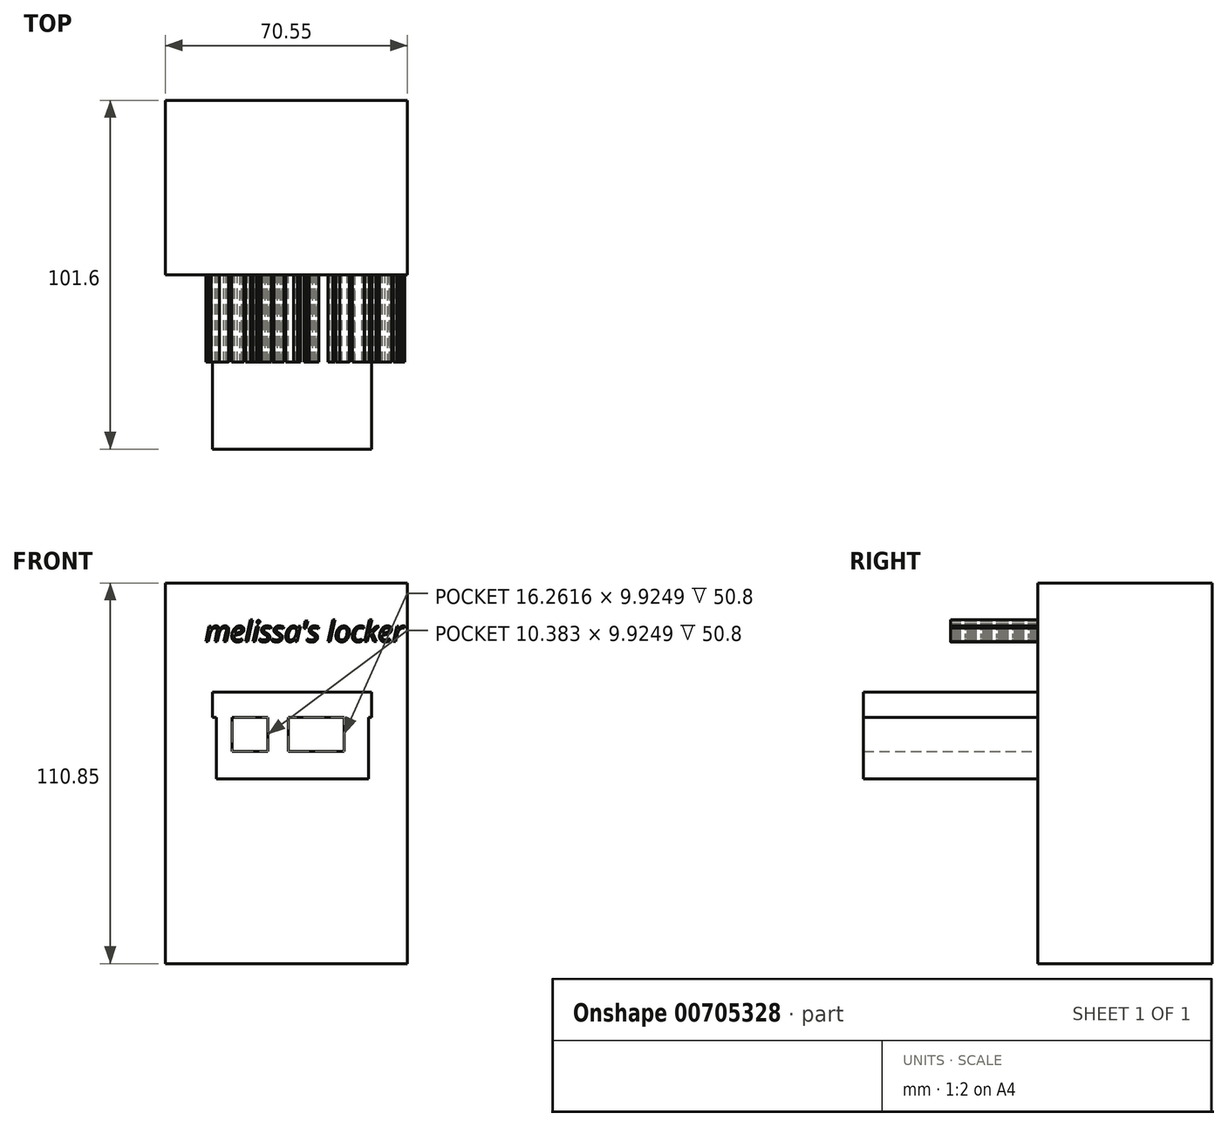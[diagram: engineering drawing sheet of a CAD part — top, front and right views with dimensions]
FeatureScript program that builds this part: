
annotation { "Feature Type Name" : "Feature", "Feature Type Description" : "" }
export const myFeature = defineFeature(function(context is Context, id is Id, definition is map)
    precondition{}
    {
        {
            var Q0;
            Q0=qCreatedBy(makeId("Front.planeOp"),FACE);
            var sketch = newSketch(context, id + "F0", { "sketchPlane" : qUnion([Q0])});
            skLineSegment(sketch, "E0.bottom", {"start": v(-52.07, 49.01) * mm, "end": v(18.48, 49.01) * mm});
            skLineSegment(sketch, "E0.top", {"start": v(-52.07, -61.84) * mm, "end": v(18.48, -61.84) * mm});
            skLineSegment(sketch, "E0.left", {"start": v(-52.07, 49.01) * mm, "end": v(-52.07, -61.84) * mm});
            skLineSegment(sketch, "E0.right", {"start": v(18.48, 49.01) * mm, "end": v(18.48, -61.84) * mm});
            skSolve(sketch);
        }
        {
            var Q0;
            Q0=makeQuery(id+"F0.imprint","IMPRINT",FACE,{"disambiguationData":[TD([[makeQuery(id+"F0.imprint","IMPRINT",EDGE,{"derivedFrom":sQuery(id+"F0.wireOp",EDGE,"E0.bottom")}),-1.0]])]});
            extrude(context, id + "F1", {"entities" : qUnion([Q0]), "depth" : 25.4 * mm, "offsetDistance" : 25.4 * mm});
        }
        {
            var Q0;
            Q0=makeQuery(id+"F1.opExtrude","CAP_FACE",FACE,{"disambiguationData":[OSD([sQuery(id+"F0.wireOp",EDGE,"E0.bottom"),sQuery(id+"F0.wireOp",EDGE,"E0.top"),sQuery(id+"F0.wireOp",EDGE,"E0.left"),sQuery(id+"F0.wireOp",EDGE,"E0.right")])],"isStart":false});
            extrude(context, id + "F2", {"entities" : qUnion([Q0]), "operationType" : NewBodyOperationType.ADD, "depth" : 25.4 * mm, "offsetDistance" : 25.4 * mm});
        }
        {
            var Q0;
            Q0=makeQuery(id+"F2.opExtrude","CAP_FACE",FACE,{"disambiguationData":[OSD([sQuery(id+"F0.wireOp",EDGE,"E0.bottom"),sQuery(id+"F0.wireOp",EDGE,"E0.top"),sQuery(id+"F0.wireOp",EDGE,"E0.left"),sQuery(id+"F0.wireOp",EDGE,"E0.right")])],"isStart":false});
            var sketch = newSketch(context, id + "F3", { "sketchPlane" : qUnion([Q0])});
            skLineSegment(sketch, "E1.bottom", {"start": v(-38.33, 17.25) * mm, "end": v(8.1, 17.25) * mm});
            skLineSegment(sketch, "E1.top", {"start": v(-38.33, 9.92) * mm, "end": v(8.1, 9.92) * mm});
            skLineSegment(sketch, "E1.left", {"start": v(-38.33, 17.25) * mm, "end": v(-38.33, 9.92) * mm});
            skLineSegment(sketch, "E1.right", {"start": v(8.1, 17.25) * mm, "end": v(8.1, 9.92) * mm});
            skSolve(sketch);
        }
        {
            var Q0;
            Q0=makeQuery(id+"F3.imprint","IMPRINT",FACE,{"disambiguationData":[TD([[makeQuery(id+"F3.imprint","IMPRINT",EDGE,{"derivedFrom":sQuery(id+"F3.wireOp",EDGE,"E1.bottom")}),-1.0]])]});
            extrude(context, id + "F4", {"entities" : qUnion([Q0]), "operationType" : NewBodyOperationType.ADD, "depth" : 25.4 * mm, "offsetDistance" : 25.4 * mm});
        }
        {
            var Q0;
            Q0=makeQuery(id+"F4.opExtrude","CAP_FACE",FACE,{"disambiguationData":[OSD([sQuery(id+"F3.wireOp",EDGE,"E1.bottom"),sQuery(id+"F3.wireOp",EDGE,"E1.top"),sQuery(id+"F3.wireOp",EDGE,"E1.left"),sQuery(id+"F3.wireOp",EDGE,"E1.right")])],"isStart":false});
            extrude(context, id + "F5", {"entities" : qUnion([Q0]), "operationType" : NewBodyOperationType.ADD, "depth" : 25.4 * mm, "offsetDistance" : 25.4 * mm});
        }
        {
            var Q0;
            Q0=makeQuery(id+"F2.opExtrude","CAP_FACE",FACE,{"disambiguationData":[OSD([sQuery(id+"F0.wireOp",EDGE,"E0.bottom"),sQuery(id+"F0.wireOp",EDGE,"E0.top"),sQuery(id+"F0.wireOp",EDGE,"E0.left"),sQuery(id+"F0.wireOp",EDGE,"E0.right")])],"isStart":false});
            var sketch = newSketch(context, id + "F6", { "sketchPlane" : qUnion([Q0])});
            skLineSegment(sketch, "E2.bottom", {"start": v(-37.1, 0) * mm, "end": v(7.18, 0) * mm});
            skLineSegment(sketch, "E2.top", {"start": v(-37.1, -8.1) * mm, "end": v(7.18, -8.1) * mm});
            skLineSegment(sketch, "E2.left", {"start": v(-37.1, 0) * mm, "end": v(-37.1, -8.1) * mm});
            skLineSegment(sketch, "E2.right", {"start": v(7.18, 0) * mm, "end": v(7.18, -8.1) * mm});
            skSolve(sketch);
        }
        {
            var Q0;
            Q0=makeQuery(id+"F6.imprint","IMPRINT",FACE,{"disambiguationData":[TD([[makeQuery(id+"F6.imprint","IMPRINT",EDGE,{"derivedFrom":sQuery(id+"F6.wireOp",EDGE,"E2.bottom")}),-1.0]])]});
            extrude(context, id + "F7", {"entities" : qUnion([Q0]), "operationType" : NewBodyOperationType.ADD, "depth" : 25.4 * mm, "offsetDistance" : 25.4 * mm});
        }
        {
            var Q0;
            Q0=makeQuery(id+"F7.opExtrude","CAP_FACE",FACE,{"disambiguationData":[OSD([sQuery(id+"F6.wireOp",EDGE,"E2.bottom"),sQuery(id+"F6.wireOp",EDGE,"E2.top"),sQuery(id+"F6.wireOp",EDGE,"E2.left"),sQuery(id+"F6.wireOp",EDGE,"E2.right")])],"isStart":false});
            extrude(context, id + "F8", {"entities" : qUnion([Q0]), "operationType" : NewBodyOperationType.ADD, "depth" : 25.4 * mm, "offsetDistance" : 25.4 * mm});
        }
        {
            var Q0;
            Q0=makeQuery(id+"F2.opExtrude","CAP_FACE",FACE,{"disambiguationData":[OSD([sQuery(id+"F0.wireOp",EDGE,"E0.bottom"),sQuery(id+"F0.wireOp",EDGE,"E0.top"),sQuery(id+"F0.wireOp",EDGE,"E0.left"),sQuery(id+"F0.wireOp",EDGE,"E0.right")])],"isStart":false});
            var sketch = newSketch(context, id + "F9", { "sketchPlane" : qUnion([Q0])});
            skLineSegment(sketch, "E3.bottom", {"start": v(-31.3, 9.92) * mm, "end": v(-26.42, 9.92) * mm});
            skLineSegment(sketch, "E3.top", {"start": v(-31.3, 0) * mm, "end": v(-26.42, 0) * mm});
            skLineSegment(sketch, "E3.left", {"start": v(-31.3, 9.92) * mm, "end": v(-31.3, 0) * mm});
            skLineSegment(sketch, "E3.right", {"start": v(-26.42, 9.92) * mm, "end": v(-26.42, 0) * mm});
            skLineSegment(sketch, "E4.bottom", {"start": v(-15.12, 9.92) * mm, "end": v(-9, 9.92) * mm});
            skLineSegment(sketch, "E4.top", {"start": v(-15.12, 0) * mm, "end": v(-9, 0) * mm});
            skLineSegment(sketch, "E4.left", {"start": v(-15.12, 9.92) * mm, "end": v(-15.12, 0) * mm});
            skLineSegment(sketch, "E4.right", {"start": v(-9, 9.92) * mm, "end": v(-9, 0) * mm});
            skLineSegment(sketch, "E5.bottom", {"start": v(0, 9.92) * mm, "end": v(7.18, 9.92) * mm});
            skLineSegment(sketch, "E5.top", {"start": v(0, 0) * mm, "end": v(7.18, 0) * mm});
            skLineSegment(sketch, "E5.left", {"start": v(0, 9.92) * mm, "end": v(0, 0) * mm});
            skLineSegment(sketch, "E5.right", {"start": v(7.18, 9.92) * mm, "end": v(7.18, 0) * mm});
            skSolve(sketch);
        }
        {
            var Q0;
            Q0=makeQuery(id+"F9.imprint","IMPRINT",FACE,{"disambiguationData":[TD([[makeQuery(id+"F9.imprint","IMPRINT",EDGE,{"derivedFrom":sQuery(id+"F9.wireOp",EDGE,"E5.bottom")}),-1.0]])]});
            extrude(context, id + "F10", {"entities" : qUnion([Q0]), "operationType" : NewBodyOperationType.ADD, "depth" : 25.4 * mm, "offsetDistance" : 25.4 * mm});
        }
        {
            var Q0;
            Q0=makeQuery(id+"F10.opExtrude","CAP_FACE",FACE,{"disambiguationData":[OSD([sQuery(id+"F9.wireOp",EDGE,"E5.bottom"),sQuery(id+"F9.wireOp",EDGE,"E5.top"),sQuery(id+"F9.wireOp",EDGE,"E5.left"),sQuery(id+"F9.wireOp",EDGE,"E5.right")])],"isStart":false});
            extrude(context, id + "F11", {"entities" : qUnion([Q0]), "operationType" : NewBodyOperationType.ADD, "depth" : 25.4 * mm, "offsetDistance" : 25.4 * mm});
        }
        {
            var Q0;
            Q0=makeQuery(id+"F2.opExtrude","CAP_FACE",FACE,{"disambiguationData":[OSD([sQuery(id+"F0.wireOp",EDGE,"E0.bottom"),sQuery(id+"F0.wireOp",EDGE,"E0.top"),sQuery(id+"F0.wireOp",EDGE,"E0.left"),sQuery(id+"F0.wireOp",EDGE,"E0.right")])],"isStart":false});
            var sketch = newSketch(context, id + "F12", { "sketchPlane" : qUnion([Q0])});
            skLineSegment(sketch, "E6.bottom", {"start": v(-35.88, 9.92) * mm, "end": v(-37.1, 9.92) * mm});
            skLineSegment(sketch, "E6.top", {"start": v(-35.88, 0) * mm, "end": v(-37.1, 0) * mm});
            skLineSegment(sketch, "E7.bottom", {"start": v(-37.1, 9.92) * mm, "end": v(-32.52, 9.92) * mm});
            skLineSegment(sketch, "E7.top", {"start": v(-37.1, 0) * mm, "end": v(-32.52, 0) * mm});
            skLineSegment(sketch, "E7.left", {"start": v(-37.1, 9.92) * mm, "end": v(-37.1, 0) * mm});
            skLineSegment(sketch, "E7.right", {"start": v(-32.52, 9.92) * mm, "end": v(-32.52, 0) * mm});
            skSolve(sketch);
        }
        {
            var Q0;
            {var subQ3=sQuery(id+"F12.wireOp",EDGE,"E7.left");Q0=makeQuery(id+"F12.imprint","IMPRINT",FACE,{"disambiguationData":[TD([[makeQuery(id+"F12.imprint","IMPRINT",EDGE,{"derivedFrom":subQ3}),1.0]])]});}
            extrude(context, id + "F13", {"entities" : qUnion([Q0]), "operationType" : NewBodyOperationType.ADD, "depth" : 25.4 * mm, "offsetDistance" : 25.4 * mm});
        }
        {
            var Q0;
            Q0=makeQuery(id+"F13.opExtrude","CAP_FACE",FACE,{"disambiguationData":[OSD([sQuery(id+"F12.wireOp",EDGE,"E7.bottom"),sQuery(id+"F12.wireOp",EDGE,"E7.top"),sQuery(id+"F12.wireOp",EDGE,"E7.left"),sQuery(id+"F12.wireOp",EDGE,"E7.right")])],"isStart":false});
            extrude(context, id + "F14", {"entities" : qUnion([Q0]), "operationType" : NewBodyOperationType.ADD, "depth" : 25.4 * mm, "offsetDistance" : 25.4 * mm});
        }
        {
            var Q0;
            {var subQ0=sQuery(id+"F6.wireOp",EDGE,"E2.bottom");Q0=makeQuery(id+"F13.boolean.opBoolean","SPLIT",FACE,{"disambiguationData":[TD([makeQuery(id+"F7.opExtrude","SWEPT_FACE",FACE,{"disambiguationData":[OSD([subQ0])]})])],"derivedFrom":makeQuery(id+"F2.opExtrude","CAP_FACE",FACE,{"disambiguationData":[OSD([sQuery(id+"F0.wireOp",EDGE,"E0.bottom"),sQuery(id+"F0.wireOp",EDGE,"E0.top"),sQuery(id+"F0.wireOp",EDGE,"E0.left"),sQuery(id+"F0.wireOp",EDGE,"E0.right")])],"isStart":false})});}
            var sketch = newSketch(context, id + "F15", { "sketchPlane" : qUnion([Q0])});
            skLineSegment(sketch, "E8.bottom", {"start": v(-16.26, 9.92) * mm, "end": v(-22.14, 9.92) * mm});
            skLineSegment(sketch, "E8.top", {"start": v(-16.26, 0) * mm, "end": v(-22.14, 0) * mm});
            skLineSegment(sketch, "E8.left", {"start": v(-16.26, 9.92) * mm, "end": v(-16.26, 0) * mm});
            skLineSegment(sketch, "E8.right", {"start": v(-22.14, 9.92) * mm, "end": v(-22.14, 0) * mm});
            skSolve(sketch);
        }
        {
            var Q0;
            Q0=makeQuery(id+"F15.imprint","IMPRINT",FACE,{"disambiguationData":[TD([[makeQuery(id+"F15.imprint","IMPRINT",EDGE,{"derivedFrom":sQuery(id+"F15.wireOp",EDGE,"E8.bottom")}),-1.0]])]});
            extrude(context, id + "F16", {"entities" : qUnion([Q0]), "operationType" : NewBodyOperationType.ADD, "depth" : 25.4 * mm, "offsetDistance" : 25.4 * mm});
        }
        {
            var Q0;
            Q0=makeQuery(id+"F16.opExtrude","CAP_FACE",FACE,{"disambiguationData":[OSD([sQuery(id+"F15.wireOp",EDGE,"E8.bottom"),sQuery(id+"F15.wireOp",EDGE,"E8.top"),sQuery(id+"F15.wireOp",EDGE,"E8.left"),sQuery(id+"F15.wireOp",EDGE,"E8.right")])],"isStart":false});
            extrude(context, id + "F17", {"entities" : qUnion([Q0]), "operationType" : NewBodyOperationType.ADD, "depth" : 25.4 * mm, "offsetDistance" : 25.4 * mm});
        }
        {
            var Q0;
            {var subQ0=sQuery(id+"F6.wireOp",EDGE,"E2.bottom");var subQ1=makeQuery(id+"F7.opExtrude","SWEPT_FACE",FACE,{"disambiguationData":[OSD([subQ0])]});var subQ6=sQuery(id+"F9.wireOp",EDGE,"E5.left");var subQ7=makeQuery(id+"F10.opExtrude","SWEPT_FACE",FACE,{"disambiguationData":[OSD([subQ6])]});Q0=makeQuery(id+"F16.boolean.opBoolean","SPLIT",FACE,{"disambiguationData":[TD([subQ7])],"derivedFrom":makeQuery(id+"F13.boolean.opBoolean","SPLIT",FACE,{"disambiguationData":[TD([subQ1])],"derivedFrom":makeQuery(id+"F2.opExtrude","CAP_FACE",FACE,{"disambiguationData":[OSD([sQuery(id+"F0.wireOp",EDGE,"E0.bottom"),sQuery(id+"F0.wireOp",EDGE,"E0.top"),sQuery(id+"F0.wireOp",EDGE,"E0.left"),sQuery(id+"F0.wireOp",EDGE,"E0.right")])],"isStart":false})})});}
            var sketch = newSketch(context, id + "F18", { "sketchPlane" : qUnion([Q0])});
            skLineSegment(sketch, "E9.bottom", {"start": v(-8.13, 9.92) * mm, "end": v(-8.13, 9.92) * mm});
            skLineSegment(sketch, "E9.top", {"start": v(-8.13, 0) * mm, "end": v(-8.13, 0) * mm});
            skText(sketch, "E10", { "text": "melissa\'s locker", "fontName": "OpenSans-Italic.ttf"});
            const initialGuessF18  = {"E10": [-0.04046, 0.03191, 1, 0, 0.0061]};
            skSetInitialGuess(sketch, initialGuessF18);
            skSolve(sketch);
        }
        {
            var Q0;
            Q0 = qSketchRegion(id + "F18", true);
            extrude(context, id + "F19", {"entities" : qUnion([Q0]), "operationType" : NewBodyOperationType.ADD, "depth" : 25.4 * mm, "offsetDistance" : 25.4 * mm});
        }
    });
